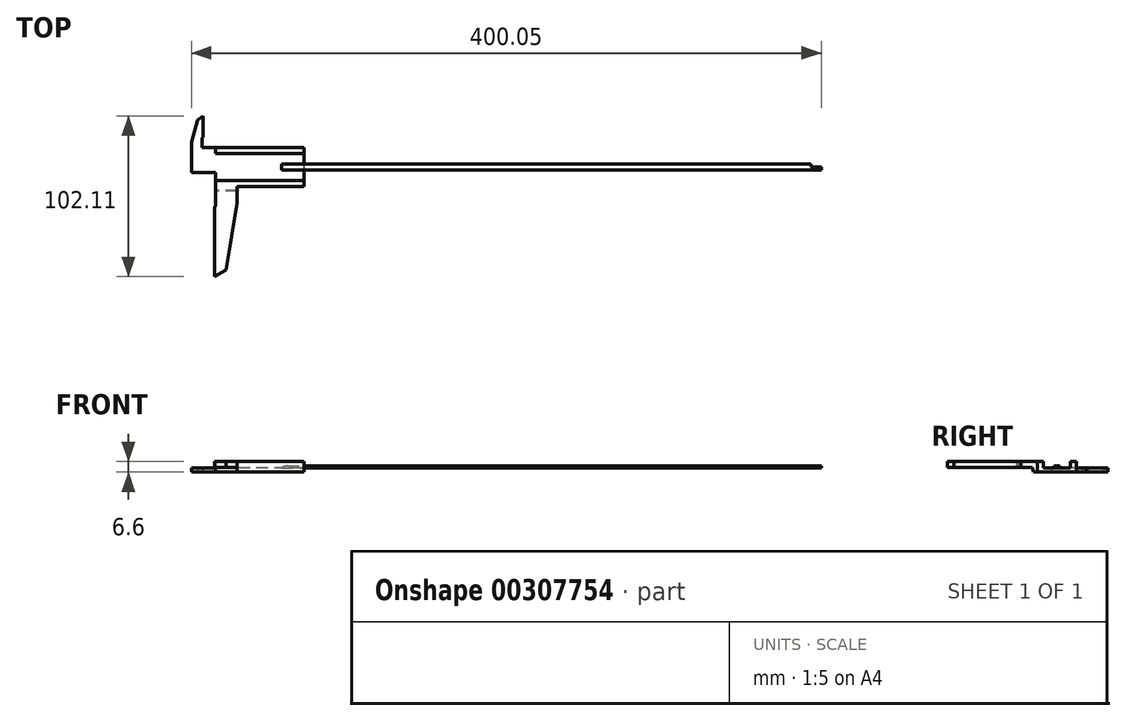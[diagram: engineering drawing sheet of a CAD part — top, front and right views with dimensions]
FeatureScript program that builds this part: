
annotation { "Feature Type Name" : "Feature", "Feature Type Description" : "" }
export const myFeature = defineFeature(function(context is Context, id is Id, definition is map)
    precondition{}
    {
        {
            var Q0;
            Q0=qCreatedBy(makeId("Top.planeOp"),FACE);
            var sketch = newSketch(context, id + "F0", { "sketchPlane" : qUnion([Q0])});
            skLineSegment(sketch, "E0.bottom", {"start": v(38.2, 0) * mm, "end": v(80.77, 0) * mm, "construction": true});
            skLineSegment(sketch, "E0.top", {"start": v(15.75, 24.94) * mm, "end": v(80.77, 24.94) * mm, "construction": true});
            skLineSegment(sketch, "E0.right", {"start": v(80.77, 0) * mm, "end": v(80.77, 24.94) * mm, "construction": true});
            skLineSegment(sketch, "E1", {"start": v(9.1, 28.24) * mm, "end": v(13.12, 42.47) * mm, "construction": true});
            skLineSegment(sketch, "E2", {"start": v(13.12, 42.47) * mm, "end": v(16.63, 44.98) * mm, "construction": true});
            skLineSegment(sketch, "E3", {"start": v(16.63, 44.98) * mm, "end": v(16.63, 31.52) * mm, "construction": true});
            skLineSegment(sketch, "E4", {"start": v(16.63, 31.52) * mm, "end": v(15.75, 30.89) * mm, "construction": true});
            skLineSegment(sketch, "E5", {"start": v(15.75, 30.89) * mm, "end": v(15.75, 24.94) * mm, "construction": true});
            skLineSegment(sketch, "E6", {"start": v(24.49, 0) * mm, "end": v(24.49, -11.89) * mm, "construction": true});
            skLineSegment(sketch, "E7", {"start": v(24.49, -11.89) * mm, "end": v(23.88, -13.19) * mm, "construction": true});
            skLineSegment(sketch, "E8", {"start": v(23.88, -13.19) * mm, "end": v(23.88, -57.13) * mm, "construction": true});
            skLineSegment(sketch, "E9", {"start": v(23.88, -57.13) * mm, "end": v(31.18, -53.02) * mm, "construction": true});
            skLineSegment(sketch, "E10", {"start": v(31.18, -53.02) * mm, "end": v(38.2, -10.41) * mm, "construction": true});
            skLineSegment(sketch, "E11", {"start": v(38.2, -10.41) * mm, "end": v(38.2, 0) * mm, "construction": true});
            skLineSegment(sketch, "E12", {"start": v(9.1, 8.94) * mm, "end": v(24.49, 8.94) * mm, "construction": true});
            skLineSegment(sketch, "E13", {"start": v(24.49, 8.94) * mm, "end": v(24.49, 0) * mm, "construction": true});
            skLineSegment(sketch, "E14", {"start": v(9.1, 8.94) * mm, "end": v(9.1, 28.24) * mm, "construction": true});
            skPoint(sketch, "E15", {"position": v(80.77, 12.47) * mm});
            skLineSegment(sketch, "E16", {"start": v(3.87, 12.47) * mm, "end": v(409.14, 12.47) * mm, "construction": true});
            skSolve(sketch);
        }
        {
            var Q0;
            Q0=qCreatedBy(makeId("Top.planeOp"),FACE);
            var sketch = newSketch(context, id + "F1", { "sketchPlane" : qUnion([Q0])});
            skLineSegment(sketch, "E17", {"start": v(80.77, 24.94) * mm, "end": v(15.75, 24.94) * mm});
            skLineSegment(sketch, "E18", {"start": v(15.75, 24.94) * mm, "end": v(15.75, 30.89) * mm});
            skLineSegment(sketch, "E19", {"start": v(15.75, 30.89) * mm, "end": v(16.63, 31.52) * mm});
            skLineSegment(sketch, "E20", {"start": v(16.63, 31.52) * mm, "end": v(16.63, 44.98) * mm});
            skLineSegment(sketch, "E21", {"start": v(16.63, 44.98) * mm, "end": v(13.12, 42.47) * mm});
            skLineSegment(sketch, "E22", {"start": v(13.12, 42.47) * mm, "end": v(9.1, 28.24) * mm});
            skLineSegment(sketch, "E23", {"start": v(9.1, 28.24) * mm, "end": v(9.1, 8.94) * mm});
            skLineSegment(sketch, "E24", {"start": v(9.1, 8.94) * mm, "end": v(24.49, 8.94) * mm});
            skLineSegment(sketch, "E25", {"start": v(24.49, 8.94) * mm, "end": v(24.49, -11.89) * mm});
            skLineSegment(sketch, "E26", {"start": v(24.49, -11.89) * mm, "end": v(23.88, -13.19) * mm});
            skLineSegment(sketch, "E27", {"start": v(23.88, -13.19) * mm, "end": v(23.88, -57.13) * mm});
            skLineSegment(sketch, "E28", {"start": v(23.88, -57.13) * mm, "end": v(31.18, -53.02) * mm});
            skLineSegment(sketch, "E29", {"start": v(31.18, -53.02) * mm, "end": v(38.2, -10.41) * mm});
            skLineSegment(sketch, "E30", {"start": v(38.2, -10.41) * mm, "end": v(38.2, 0) * mm});
            skLineSegment(sketch, "E31", {"start": v(38.2, 0) * mm, "end": v(80.77, 0) * mm});
            skLineSegment(sketch, "E32", {"start": v(80.77, 0) * mm, "end": v(80.77, 24.94) * mm});
            skSolve(sketch);
        }
        {
            var Q0;
            Q0 = qSketchRegion(id + "F1", true);
            extrude(context, id + "F2", {"entities" : qUnion([Q0]), "depth" : 6.6 * mm});
        }
        {
            var Q0;
            Q0=makeQuery(id+"F2.opExtrude","SWEPT_FACE",FACE,{"disambiguationData":[OSD([sQuery(id+"F1.wireOp",EDGE,"E23")])]});
            var sketch = newSketch(context, id + "F3", { "sketchPlane" : qUnion([Q0])});
            skLineSegment(sketch, "E33", {"start": v(5.83, 2.54) * mm, "end": v(-59.47, 2.54) * mm, "construction": true});
            skSolve(sketch);
        }
        {
            var Q0;
            {var subQ0=sQuery(id+"F1.wireOp",EDGE,"E23");Q0=makeQuery(id+"F3.imprint","IMPRINT",FACE,{"disambiguationData":[TD([[makeQuery(id+"F3.imprint","IMPRINT",EDGE,{"derivedFrom":makeQuery(id+"F2.opExtrude","CAP_EDGE",EDGE,{"disambiguationData":[OSD([subQ0])],"isStart":true})}),1.0]])]});}
            var sketch = newSketch(context, id + "F4", { "sketchPlane" : qUnion([Q0])});
            skLineSegment(sketch, "E34.bottom", {"start": v(-20.98, 8.14) * mm, "end": v(-3.96, 8.14) * mm});
            skLineSegment(sketch, "E34.top", {"start": v(-20.98, 2.54) * mm, "end": v(-3.96, 2.54) * mm});
            skLineSegment(sketch, "E34.left", {"start": v(-20.98, 8.14) * mm, "end": v(-20.98, 2.54) * mm});
            skLineSegment(sketch, "E34.right", {"start": v(-3.96, 8.14) * mm, "end": v(-3.96, 2.54) * mm});
            skPoint(sketch, "E35", {"position": v(-12.47, 2.54) * mm});
            skSolve(sketch);
        }
        {
            var Q0;
            Q0 = qSketchRegion(id + "F4", true);
            extrude(context, id + "F5", {"entities" : qUnion([Q0]), "operationType" : NewBodyOperationType.REMOVE, "endBound" : BoundingType.THROUGH_ALL, "oppositeDirection" : true, "depth" : 25.4 * mm});
        }
        {
            var Q0;
            Q0=qCreatedBy(makeId("Front.planeOp"),FACE);
            var sketch = newSketch(context, id + "F6", { "sketchPlane" : qUnion([Q0])});
            skLineSegment(sketch, "E36.bottom", {"start": v(24.49, 2.54) * mm, "end": v(8.13, 2.54) * mm});
            skLineSegment(sketch, "E36.top", {"start": v(24.49, 6.85) * mm, "end": v(8.13, 6.85) * mm});
            skLineSegment(sketch, "E36.left", {"start": v(24.49, 2.54) * mm, "end": v(24.49, 6.85) * mm});
            skLineSegment(sketch, "E36.right", {"start": v(8.13, 2.54) * mm, "end": v(8.13, 6.85) * mm});
            skSolve(sketch);
        }
        {
            var Q0;
            Q0 = qSketchRegion(id + "F6", true);
            extrude(context, id + "F7", {"entities" : qUnion([Q0]), "operationType" : NewBodyOperationType.REMOVE, "endBound" : BoundingType.THROUGH_ALL, "oppositeDirection" : true, "depth" : 25.4 * mm});
        }
        {
            var Q0;
            Q0=makeQuery(id+"F2.opExtrude","SWEPT_FACE",FACE,{"disambiguationData":[OSD([sQuery(id+"F1.wireOp",EDGE,"E27")])]});
            var sketch = newSketch(context, id + "F8", { "sketchPlane" : qUnion([Q0])});
            skLineSegment(sketch, "E37", {"start": v(57.13, 2.8) * mm, "end": v(2.9, 2.8) * mm});
            skLineSegment(sketch, "E38", {"start": v(2.9, 2.8) * mm, "end": v(2.03, -1.48) * mm});
            skLineSegment(sketch, "E39", {"start": v(2.03, -1.48) * mm, "end": v(57.13, -1.48) * mm});
            skLineSegment(sketch, "E40", {"start": v(57.13, -1.48) * mm, "end": v(57.13, 2.8) * mm});
            skSolve(sketch);
        }
        {
            var Q0;
            Q0 = qSketchRegion(id + "F8", true);
            extrude(context, id + "F9", {"entities" : qUnion([Q0]), "operationType" : NewBodyOperationType.REMOVE, "endBound" : BoundingType.THROUGH_ALL, "oppositeDirection" : true, "depth" : 25.4 * mm});
        }
        {
            var Q0;
            Q0=makeQuery(id+"F7.boolean.opBoolean","MERGE",FACE,{"derivedFrom":[makeQuery(id+"F5.boolean.opBoolean","COPY",FACE,{"derivedFrom":makeQuery(id+"F5.opExtrude","SWEPT_FACE",FACE,{"disambiguationData":[OSD([sQuery(id+"F4.wireOp",EDGE,"E34.top")])]})}),makeQuery(id+"F7.opExtrude","SWEPT_FACE",FACE,{"disambiguationData":[OSD([sQuery(id+"F6.wireOp",EDGE,"E36.bottom")])]})]});
            var sketch = newSketch(context, id + "F10", { "sketchPlane" : qUnion([Q0])});
            skLineSegment(sketch, "E41.bottom", {"start": v(66.27, 10.62) * mm, "end": v(409.14, 10.62) * mm});
            skLineSegment(sketch, "E41.top", {"start": v(66.27, 14.33) * mm, "end": v(409.14, 14.33) * mm});
            skLineSegment(sketch, "E41.left", {"start": v(66.27, 10.62) * mm, "end": v(66.27, 14.33) * mm});
            skLineSegment(sketch, "E41.right", {"start": v(409.14, 10.62) * mm, "end": v(409.14, 14.33) * mm});
            skPoint(sketch, "E42", {"position": v(66.27, 12.47) * mm});
            skPoint(sketch, "E43", {"position": v(409.14, 12.47) * mm});
            skSolve(sketch);
        }
        {
            var Q0;
            Q0 = qSketchRegion(id + "F10", true);
            extrude(context, id + "F11", {"entities" : qUnion([Q0]), "operationType" : NewBodyOperationType.ADD, "depth" : 1.27 * mm});
        }
        {
            var Q0;
            Q0=makeQuery(id+"F11.opExtrude","CAP_EDGE",EDGE,{"disambiguationData":[OSD([sQuery(id+"F10.wireOp",EDGE,"E41.left")])],"isStart":false});
            fillet(context, id + "F12", {"entities" : qUnion([Q0]), "radius" : 6.35 * mm, "tangentPropagation" : true, "allowEdgeOverflow" : false});
        }
        {
            var Q0;
            Q0=makeQuery(id+"F11.opExtrude","CAP_FACE",FACE,{"disambiguationData":[OSD([sQuery(id+"F10.wireOp",EDGE,"E41.bottom"),sQuery(id+"F10.wireOp",EDGE,"E41.top"),sQuery(id+"F10.wireOp",EDGE,"E41.left"),sQuery(id+"F10.wireOp",EDGE,"E41.right")])],"isStart":true});
            var sketch = newSketch(context, id + "F13", { "sketchPlane" : qUnion([Q0])});
            skLineSegment(sketch, "E44", {"start": v(402.44, -13.6) * mm, "end": v(402.44, -14.33) * mm});
            skLineSegment(sketch, "E45", {"start": v(409.14, -12.55) * mm, "end": v(403.49, -12.55) * mm});
            skPoint(sketch, "E46.visualSharp", {"position": v(402.44, -12.55) * mm});
            skLineSegment(sketch, "E47", {"start": v(402.44, -14.33) * mm, "end": v(409.48, -15.1) * mm});
            skLineSegment(sketch, "E48", {"start": v(409.48, -15.1) * mm, "end": v(409.14, -12.55) * mm});
            skArc(sketch, "E49", {"start": v(403.49, -12.55) * mm, "mid": v(402.75, -12.85) * mm, "end": v(402.44, -13.6) * mm});
            skSolve(sketch);
        }
        {
            var Q0;
            Q0 = qSketchRegion(id + "F13", true);
            extrude(context, id + "F14", {"entities" : qUnion([Q0]), "operationType" : NewBodyOperationType.REMOVE, "endBound" : BoundingType.THROUGH_ALL, "oppositeDirection" : true, "depth" : 25.4 * mm});
        }
    });
